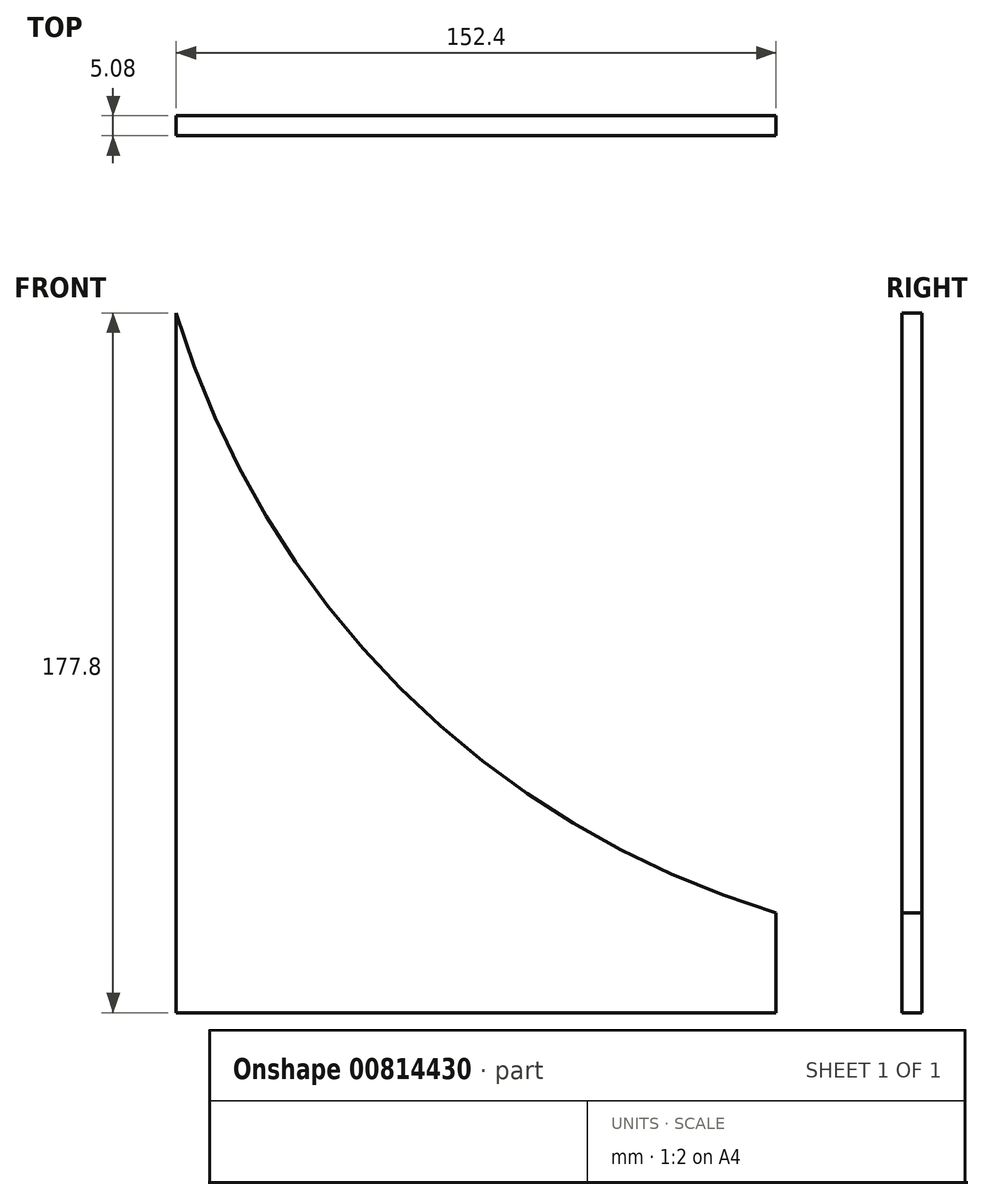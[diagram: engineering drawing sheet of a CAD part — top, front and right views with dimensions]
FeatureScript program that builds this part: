
annotation { "Feature Type Name" : "Feature", "Feature Type Description" : "" }
export const myFeature = defineFeature(function(context is Context, id is Id, definition is map)
    precondition{}
    {
        {
            var Q0;
            Q0=qCreatedBy(makeId("Front.planeOp"),FACE);
            var sketch = newSketch(context, id + "F0", { "sketchPlane" : qUnion([Q0])});
            skLineSegment(sketch, "E0.bottom", {"start": v(-133.7, -54.15) * mm, "end": v(18.7, -54.15) * mm});
            skLineSegment(sketch, "E0.top", {"start": v(-133.7, 98.25) * mm, "end": v(18.7, 98.25) * mm});
            skLineSegment(sketch, "E0.left", {"start": v(-133.7, -54.15) * mm, "end": v(-133.7, 98.25) * mm});
            skLineSegment(sketch, "E0.right", {"start": v(18.7, -54.15) * mm, "end": v(18.7, 98.25) * mm});
            skSolve(sketch);
        }
        {
            var Q0;
            Q0=makeQuery(id+"F0.imprint","IMPRINT",FACE,{"disambiguationData":[TD([[makeQuery(id+"F0.imprint","IMPRINT",EDGE,{"derivedFrom":sQuery(id+"F0.wireOp",EDGE,"E0.bottom")}),1.0]])]});
            extrude(context, id + "F1", {"entities" : qUnion([Q0]), "depth" : 5.08 * mm, "offsetDistance" : 25.4 * mm});
        }
        {
            var Q0;
            Q0=makeQuery(id+"F1.opExtrude","CAP_FACE",FACE,{"disambiguationData":[OSD([sQuery(id+"F0.wireOp",EDGE,"E0.bottom"),sQuery(id+"F0.wireOp",EDGE,"E0.top"),sQuery(id+"F0.wireOp",EDGE,"E0.left"),sQuery(id+"F0.wireOp",EDGE,"E0.right")])],"isStart":false});
            var sketch = newSketch(context, id + "F2", { "sketchPlane" : qUnion([Q0])});
            skArc(sketch, "E1", {"start": v(-133.7, 98.25) * mm, "mid": v(-76.68, 2.87) * mm, "end": v(18.7, -54.15) * mm});
            skSolve(sketch);
        }
        {
            var Q0;
            Q0=makeQuery(id+"F2.imprint","IMPRINT",FACE,{"disambiguationData":[TD([[makeQuery(id+"F2.imprint","IMPRINT",EDGE,{"derivedFrom":sQuery(id+"F2.wireOp",EDGE,"E1")}),1.0]])]});
            extrude(context, id + "F3", {"entities" : qUnion([Q0]), "operationType" : NewBodyOperationType.REMOVE, "oppositeDirection" : true, "depth" : 5.08 * mm, "offsetDistance" : 25.4 * mm});
        }
        {
            var Q0;
            Q0=makeQuery(id+"F1.opExtrude","SWEPT_FACE",FACE,{"disambiguationData":[OSD([sQuery(id+"F0.wireOp",EDGE,"E0.bottom")])]});
            extrude(context, id + "F4", {"entities" : qUnion([Q0]), "operationType" : NewBodyOperationType.ADD, "depth" : 25.4 * mm, "offsetDistance" : 25.4 * mm});
        }
    });
